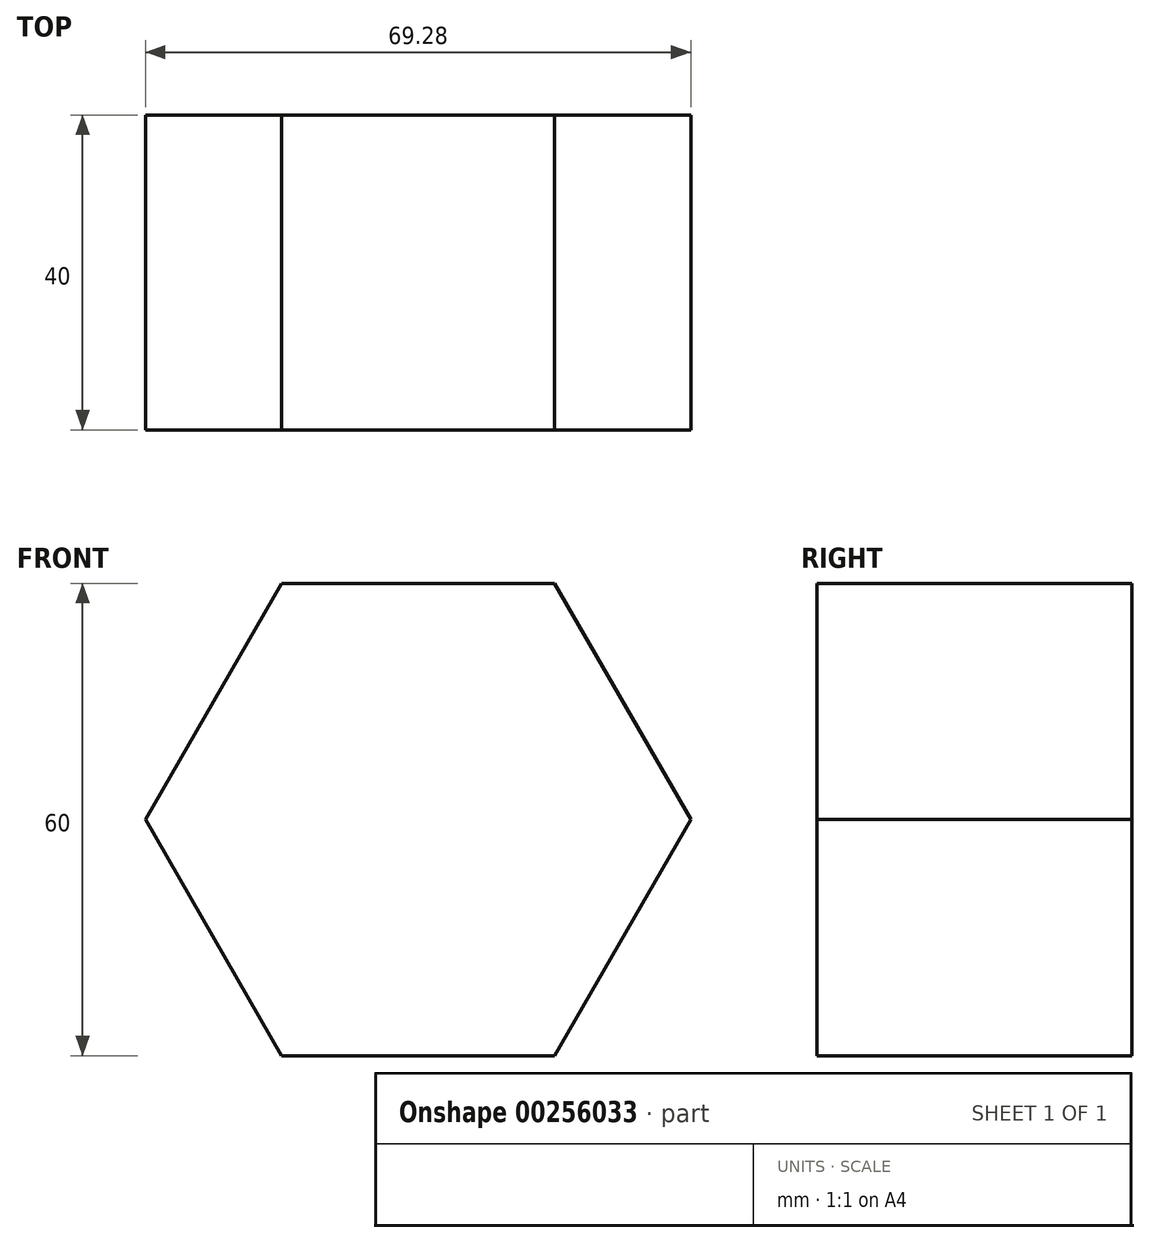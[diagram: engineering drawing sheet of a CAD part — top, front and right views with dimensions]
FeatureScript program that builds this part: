
annotation { "Feature Type Name" : "Feature", "Feature Type Description" : "" }
export const myFeature = defineFeature(function(context is Context, id is Id, definition is map)
    precondition{}
    {
        {
            var Q0;
            Q0=qCreatedBy(makeId("Front.planeOp"),FACE);
            var sketch = newSketch(context, id + "F0", { "sketchPlane" : qUnion([Q0])});
            skCircle(sketch, "E0", {"center": v(0, 0) * mm, "radius": 30 * mm});
            skCircle(sketch, "E1.cCircle", {"center": v(0, 0) * mm, "radius": 30 * mm, "construction": true});
            skLineSegment(sketch, "E1.0", {"start": v(17.32, -30) * mm, "end": v(-17.32, -30) * mm});
            skLineSegment(sketch, "E1.1", {"start": v(-17.32, -30) * mm, "end": v(-34.64, 0) * mm});
            skLineSegment(sketch, "E1.2", {"start": v(-34.64, 0) * mm, "end": v(-17.32, 30) * mm});
            skLineSegment(sketch, "E1.3", {"start": v(-17.32, 30) * mm, "end": v(17.32, 30) * mm});
            skLineSegment(sketch, "E1.4", {"start": v(17.32, 30) * mm, "end": v(34.64, 0) * mm});
            skLineSegment(sketch, "E1.5", {"start": v(34.64, 0) * mm, "end": v(17.32, -30) * mm});
            skPoint(sketch, "E1.0.midPoint", {"position": v(0, -30) * mm});
            skSolve(sketch);
        }
        {
            var Q0;
            {var subQ0=sQuery(id+"F0.wireOp",EDGE,"E1.3");var subQ1=sQuery(id+"F0.wireOp",EDGE,"E0");var subQ2=makeQuery(id+"F0.imprint","INTERSECT",VERTEX,{"derivedFrom":[subQ1,subQ0]});Q0=makeQuery(id+"F0.imprint","IMPRINT",FACE,{"disambiguationData":[TD([[makeQuery(id+"F0.imprint","IMPRINT",EDGE,{"disambiguationData":[TD([[subQ2,1.0]])],"derivedFrom":subQ1}),-1.0]])]});}
            var Q1;
            {var subQ0=sQuery(id+"F0.wireOp",EDGE,"E1.3");var subQ1=sQuery(id+"F0.wireOp",EDGE,"E0");var subQ2=makeQuery(id+"F0.imprint","INTERSECT",VERTEX,{"derivedFrom":[subQ1,subQ0]});Q1=makeQuery(id+"F0.imprint","IMPRINT",FACE,{"disambiguationData":[TD([[makeQuery(id+"F0.imprint","IMPRINT",EDGE,{"disambiguationData":[TD([[subQ2,-1.0]])],"derivedFrom":subQ1}),-1.0]])]});}
            var Q2;
            {var subQ0=sQuery(id+"F0.wireOp",EDGE,"E1.2");var subQ1=sQuery(id+"F0.wireOp",EDGE,"E0");var subQ2=makeQuery(id+"F0.imprint","INTERSECT",VERTEX,{"derivedFrom":[subQ1,subQ0]});Q2=makeQuery(id+"F0.imprint","IMPRINT",FACE,{"disambiguationData":[TD([[makeQuery(id+"F0.imprint","IMPRINT",EDGE,{"disambiguationData":[TD([[subQ2,-1.0]])],"derivedFrom":subQ1}),-1.0]])]});}
            var Q3;
            {var subQ0=sQuery(id+"F0.wireOp",EDGE,"E1.1");var subQ1=sQuery(id+"F0.wireOp",EDGE,"E0");var subQ2=makeQuery(id+"F0.imprint","INTERSECT",VERTEX,{"derivedFrom":[subQ1,subQ0]});Q3=makeQuery(id+"F0.imprint","IMPRINT",FACE,{"disambiguationData":[TD([[makeQuery(id+"F0.imprint","IMPRINT",EDGE,{"disambiguationData":[TD([[subQ2,-1.0]])],"derivedFrom":subQ1}),-1.0]])]});}
            var Q4;
            {var subQ0=sQuery(id+"F0.wireOp",EDGE,"E1.0");var subQ1=sQuery(id+"F0.wireOp",EDGE,"E0");var subQ2=makeQuery(id+"F0.imprint","INTERSECT",VERTEX,{"derivedFrom":[subQ1,subQ0]});Q4=makeQuery(id+"F0.imprint","IMPRINT",FACE,{"disambiguationData":[TD([[makeQuery(id+"F0.imprint","IMPRINT",EDGE,{"disambiguationData":[TD([[subQ2,-1.0]])],"derivedFrom":subQ1}),-1.0]])]});}
            var Q5;
            {var subQ0=sQuery(id+"F0.wireOp",EDGE,"E1.4");var subQ1=sQuery(id+"F0.wireOp",EDGE,"E0");var subQ2=makeQuery(id+"F0.imprint","INTERSECT",VERTEX,{"derivedFrom":[subQ1,subQ0]});Q5=makeQuery(id+"F0.imprint","IMPRINT",FACE,{"disambiguationData":[TD([[makeQuery(id+"F0.imprint","IMPRINT",EDGE,{"disambiguationData":[TD([[subQ2,1.0]])],"derivedFrom":subQ1}),-1.0]])]});}
            var Q6;
            {var subQ0=sQuery(id+"F0.wireOp",EDGE,"E0");var subQ4=makeQuery(id+"F0.imprint","INTERSECT",VERTEX,{"derivedFrom":[subQ0,sQuery(id+"F0.wireOp",EDGE,"E1.3")]});Q6=makeQuery(id+"F0.imprint","IMPRINT",FACE,{"disambiguationData":[TD([[makeQuery(id+"F0.imprint","IMPRINT",EDGE,{"disambiguationData":[TD([[subQ4,1.0]])],"derivedFrom":subQ0}),1.0]])]});}
            extrude(context, id + "F1", {"entities" : qUnion([Q0, Q1, Q2, Q3, Q4, Q5, Q6]), "oppositeDirection" : true, "depth" : 40 * mm});
        }
    });
